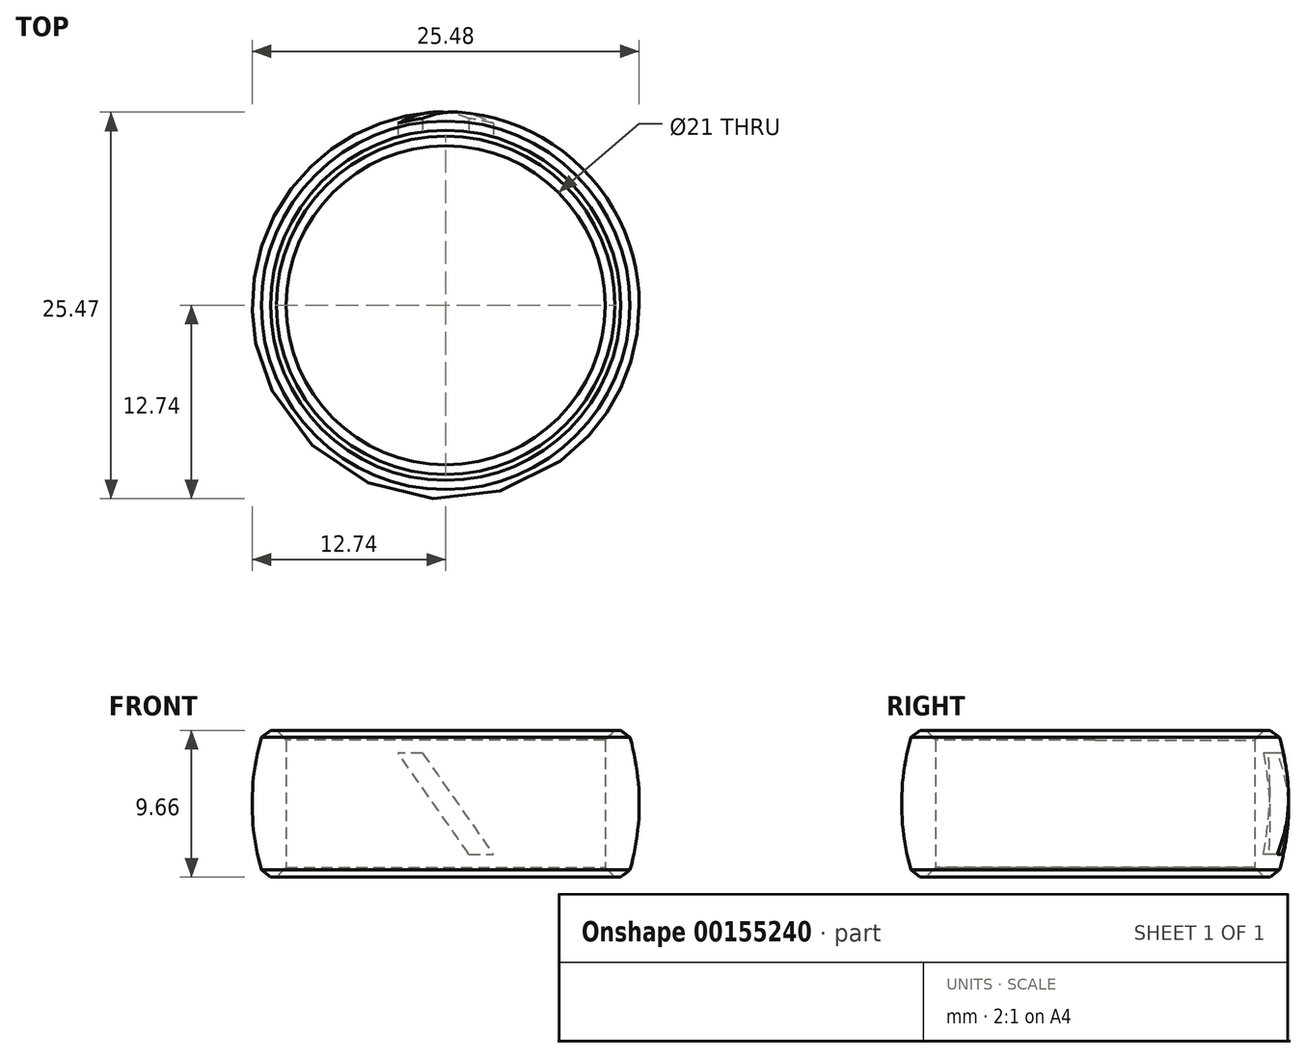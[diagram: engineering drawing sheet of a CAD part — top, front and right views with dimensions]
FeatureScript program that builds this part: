
annotation { "Feature Type Name" : "Feature", "Feature Type Description" : "" }
export const myFeature = defineFeature(function(context is Context, id is Id, definition is map)
    precondition{}
    {
        {
            var Q0;
            Q0=qCreatedBy(makeId("Right.planeOp"),FACE);
            var sketch = newSketch(context, id + "F0", { "sketchPlane" : qUnion([Q0])});
            skLineSegment(sketch, "E0", {"start": v(0, -18.8) * mm, "end": v(0, 21.5) * mm});
            skSolve(sketch);
        }
        {
            var Q0;
            Q0=qCreatedBy(makeId("Right.planeOp"),FACE);
            var sketch = newSketch(context, id + "F1", { "sketchPlane" : qUnion([Q0])});
            skLineSegment(sketch, "E1", {"start": v(10.5, 0) * mm, "end": v(10.5, 4.82) * mm});
            skLineSegment(sketch, "E2.MirrorCS", {"start": v(10.5, 0) * mm, "end": v(10.5, -4.82) * mm});
            skLineSegment(sketch, "E3", {"start": v(10.5, -4.83) * mm, "end": v(12, -4.83) * mm});
            skLineSegment(sketch, "E4", {"start": v(12, -4.83) * mm, "end": v(12, 4.83) * mm, "construction": true});
            skLineSegment(sketch, "E5", {"start": v(12, 4.83) * mm, "end": v(10.5, 4.83) * mm});
            skArc(sketch, "E6", {"start": v(12, -4.83) * mm, "mid": v(12.74, 0) * mm, "end": v(12, 4.82) * mm});
            skSolve(sketch);
        }
        {
            var Q0;
            Q0=makeQuery(id+"F1.imprint","IMPRINT",FACE,{"disambiguationData":[TD([[makeQuery(id+"F1.imprint","IMPRINT",EDGE,{"derivedFrom":sQuery(id+"F1.wireOp",EDGE,"E1")}),-1.0]])]});
            var Q1;
            Q1=sQuery(id+"F0.wireOp",EDGE,"E0");
            revolve(context, id + "F2", {"entities" : qUnion([Q0]), "axis" : qUnion([Q1]), "revolveType" : RevolveType.FULL});
        }
        {
            var Q0;
            Q0=qCreatedBy(makeId("Front.planeOp"),FACE);
            var sketch = newSketch(context, id + "F3", { "sketchPlane" : qUnion([Q0])});
            skLineSegment(sketch, "E7", {"start": v(-1.53, 3.32) * mm, "end": v(-3.13, 3.32) * mm});
            skLineSegment(sketch, "E8", {"start": v(-3.13, 3.32) * mm, "end": v(1.53, -3.32) * mm});
            skLineSegment(sketch, "E9", {"start": v(1.53, -3.32) * mm, "end": v(3.13, -3.32) * mm});
            skLineSegment(sketch, "E10", {"start": v(3.13, -3.32) * mm, "end": v(-1.53, 3.32) * mm});
            skLineSegment(sketch, "E11", {"start": v(3.13, -3.33) * mm, "end": v(-3.13, 3.32) * mm, "construction": true});
            skSolve(sketch);
        }
        {
            var Q0;
            Q0=makeQuery(id+"F3.imprint","IMPRINT",FACE,{"disambiguationData":[TD([[makeQuery(id+"F3.imprint","IMPRINT",EDGE,{"derivedFrom":sQuery(id+"F3.wireOp",EDGE,"E7")}),1.0]])]});
            extrude(context, id + "F4", {"entities" : qUnion([Q0]), "operationType" : NewBodyOperationType.REMOVE, "oppositeDirection" : true, "depth" : 25 * mm});
        }
        {
            var Q0;
            Q0=qCreatedBy(makeId("Top.planeOp"),FACE);
            var sketch = newSketch(context, id + "F5", { "sketchPlane" : qUnion([Q0])});
            skCircle(sketch, "E12", {"center": v(0, 0) * mm, "radius": 11.5 * mm});
            skCircle(sketch, "E13", {"center": v(0, 0) * mm, "radius": 10.5 * mm});
            skSolve(sketch);
        }
        {
            var Q0;
            Q0 = qSketchRegion(id + "F5", true);
            extrude(context, id + "F6", {"entities" : qUnion([Q0]), "operationType" : NewBodyOperationType.ADD, "endBound" : BoundingType.SYMMETRIC, "depth" : 9.65 * mm});
        }
        {
            var Q0;
            Q0=makeQuery(id+"F2.opRevolve","SWEPT_EDGE",EDGE,{"disambiguationData":[OSD([sQuery(id+"F1.wireOp",EDGE,"E4"),sQuery(id+"F1.wireOp",EDGE,"E5")])]});
            var Q1;
            Q1=makeQuery(id+"F2.opRevolve","SWEPT_EDGE",EDGE,{"disambiguationData":[OSD([sQuery(id+"F1.wireOp",EDGE,"E3"),sQuery(id+"F1.wireOp",EDGE,"E4")])]});
            var Q2;
            Q2=makeQuery(id+"F2.opRevolve","SWEPT_EDGE",EDGE,{"disambiguationData":[OSD([sQuery(id+"F1.wireOp",EDGE,"E1"),sQuery(id+"F1.wireOp",EDGE,"E5")])]});
            var Q3;
            Q3=makeQuery(id+"F2.opRevolve","SWEPT_EDGE",EDGE,{"disambiguationData":[OSD([sQuery(id+"F1.wireOp",EDGE,"E2.MirrorCS"),sQuery(id+"F1.wireOp",EDGE,"E3")])]});
            chamfer(context, id + "F7", {"entities" : qUnion([Q0, Q1, Q2, Q3]), "width" : 0.64 * mm, "tangentPropagation" : true});
        }
    });
